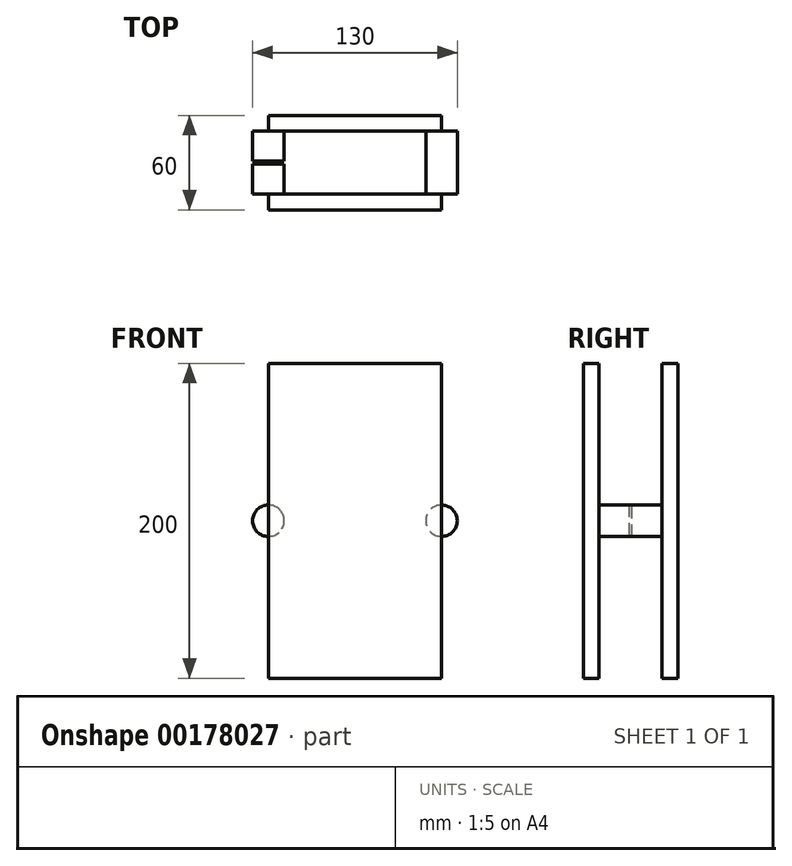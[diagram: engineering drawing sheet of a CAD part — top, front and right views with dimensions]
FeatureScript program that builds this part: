
annotation { "Feature Type Name" : "Feature", "Feature Type Description" : "" }
export const myFeature = defineFeature(function(context is Context, id is Id, definition is map)
    precondition{}
    {
        {
            var Q0;
            Q0=qCreatedBy(makeId("Front.planeOp"),FACE);
            var sketch = newSketch(context, id + "F0", { "sketchPlane" : qUnion([Q0])});
            skLineSegment(sketch, "E0.bottom", {"start": v(55, 100) * mm, "end": v(-55, 100) * mm});
            skLineSegment(sketch, "E0.top", {"start": v(55, -100) * mm, "end": v(-55, -100) * mm});
            skLineSegment(sketch, "E0.left", {"start": v(55, 100) * mm, "end": v(55, -100) * mm});
            skLineSegment(sketch, "E0.right", {"start": v(-55, 100) * mm, "end": v(-55, -100) * mm});
            skPoint(sketch, "E0.middle", {"position": v(0, 0) * mm});
            skSolve(sketch);
        }
        {
            var Q0;
            Q0 = qSketchRegion(id + "F0", true);
            extrude(context, id + "F1", {"entities" : qUnion([Q0]), "depth" : 10 * mm});
        }
        {
            var Q0;
            Q0=makeQuery(id+"F1.opExtrude","CAP_FACE",FACE,{"disambiguationData":[OSD([sQuery(id+"F0.wireOp",EDGE,"E0.bottom"),sQuery(id+"F0.wireOp",EDGE,"E0.top"),sQuery(id+"F0.wireOp",EDGE,"E0.left"),sQuery(id+"F0.wireOp",EDGE,"E0.right")])],"isStart":false});
            var sketch = newSketch(context, id + "F2", { "sketchPlane" : qUnion([Q0])});
            skCircle(sketch, "E1", {"center": v(55, 0) * mm, "radius": 10 * mm});
            skSolve(sketch);
        }
        {
            var Q0;
            Q0 = qSketchRegion(id + "F2", true);
            extrude(context, id + "F3", {"entities" : qUnion([Q0]), "operationType" : NewBodyOperationType.ADD, "depth" : 40 * mm});
        }
        {
            var Q0;
            Q0=makeQuery(id+"F3.opExtrude","CAP_FACE",FACE,{"disambiguationData":[OSD([sQuery(id+"F2.wireOp",EDGE,"E1")])],"isStart":false});
            var sketch = newSketch(context, id + "F4", { "sketchPlane" : qUnion([Q0])});
            skLineSegment(sketch, "E2.bottom", {"start": v(55, 100) * mm, "end": v(-55, 100) * mm});
            skLineSegment(sketch, "E2.top", {"start": v(55, -100) * mm, "end": v(-55, -100) * mm});
            skLineSegment(sketch, "E2.left", {"start": v(55, 100) * mm, "end": v(55, -100) * mm});
            skLineSegment(sketch, "E2.right", {"start": v(-55, 100) * mm, "end": v(-55, -100) * mm});
            skPoint(sketch, "E2.middle", {"position": v(0, 0) * mm});
            skSolve(sketch);
        }
        {
            var Q0;
            Q0 = qSketchRegion(id + "F4", true);
            extrude(context, id + "F5", {"entities" : qUnion([Q0]), "operationType" : NewBodyOperationType.ADD, "depth" : 10 * mm});
        }
        {
            var Q0;
            Q0=makeQuery(id+"F1.opExtrude","CAP_FACE",FACE,{"disambiguationData":[OSD([sQuery(id+"F0.wireOp",EDGE,"E0.bottom"),sQuery(id+"F0.wireOp",EDGE,"E0.top"),sQuery(id+"F0.wireOp",EDGE,"E0.left"),sQuery(id+"F0.wireOp",EDGE,"E0.right")])],"isStart":false});
            var sketch = newSketch(context, id + "F6", { "sketchPlane" : qUnion([Q0])});
            skCircle(sketch, "E3", {"center": v(-55, 0) * mm, "radius": 10 * mm});
            skSolve(sketch);
        }
        {
            var Q0;
            Q0 = qSketchRegion(id + "F6", true);
            extrude(context, id + "F7", {"entities" : qUnion([Q0]), "operationType" : NewBodyOperationType.ADD, "depth" : 19 * mm});
        }
        {
            var Q0;
            Q0=makeQuery(id+"F5.opExtrude","CAP_FACE",FACE,{"disambiguationData":[OSD([sQuery(id+"F4.wireOp",EDGE,"E2.bottom"),sQuery(id+"F4.wireOp",EDGE,"E2.top"),sQuery(id+"F4.wireOp",EDGE,"E2.left"),sQuery(id+"F4.wireOp",EDGE,"E2.right")])],"isStart":true});
            var sketch = newSketch(context, id + "F8", { "sketchPlane" : qUnion([Q0])});
            skCircle(sketch, "E4", {"center": v(55, 0) * mm, "radius": 10 * mm});
            skSolve(sketch);
        }
        {
            var Q0;
            Q0 = qSketchRegion(id + "F8", true);
            extrude(context, id + "F9", {"entities" : qUnion([Q0]), "operationType" : NewBodyOperationType.ADD, "depth" : 19 * mm});
        }
    });
